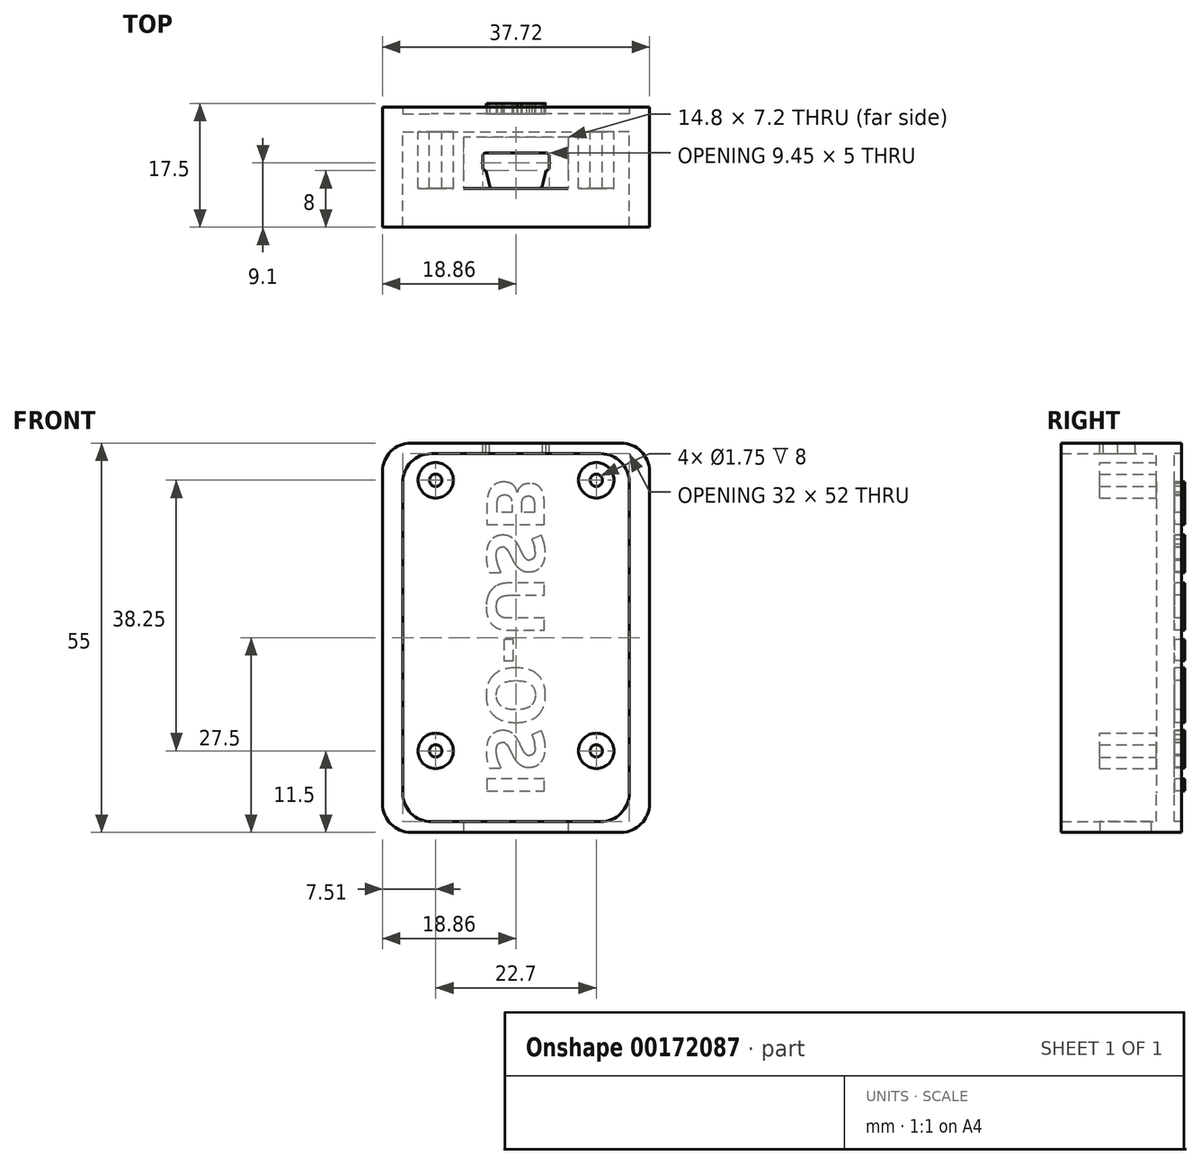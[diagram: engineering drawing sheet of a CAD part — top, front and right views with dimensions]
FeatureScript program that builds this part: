
annotation { "Feature Type Name" : "Feature", "Feature Type Description" : "" }
export const myFeature = defineFeature(function(context is Context, id is Id, definition is map)
    precondition{}
    {
        {
            var Q0;
            Q0=qCreatedBy(makeId("Front.planeOp"),FACE);
            var sketch = newSketch(context, id + "F0", { "sketchPlane" : qUnion([Q0])});
            skLineSegment(sketch, "E0.bottom", {"start": v(12, -26) * mm, "end": v(-12, -26) * mm});
            skLineSegment(sketch, "E0.top", {"start": v(12, 26) * mm, "end": v(-12, 26) * mm});
            skLineSegment(sketch, "E0.left", {"start": v(16, -22) * mm, "end": v(16, 22) * mm});
            skLineSegment(sketch, "E0.right", {"start": v(-16, -22) * mm, "end": v(-16, 22) * mm});
            skPoint(sketch, "E0.middle", {"position": v(0, 0) * mm});
            skPoint(sketch, "E1.visualSharp", {"position": v(-16, 26) * mm});
            skArc(sketch, "E1.filletArc", {"start": v(-12, 26) * mm, "mid": v(-14.83, 24.83) * mm, "end": v(-16, 22) * mm});
            skPoint(sketch, "E2.visualSharp", {"position": v(16, 26) * mm});
            skArc(sketch, "E2.filletArc", {"start": v(16, 22) * mm, "mid": v(14.83, 24.83) * mm, "end": v(12, 26) * mm});
            skPoint(sketch, "E3.visualSharp", {"position": v(16, -26) * mm});
            skArc(sketch, "E3.filletArc", {"start": v(12, -26) * mm, "mid": v(14.83, -24.83) * mm, "end": v(16, -22) * mm});
            skPoint(sketch, "E4.visualSharp", {"position": v(-16, -26) * mm});
            skArc(sketch, "E4.filletArc", {"start": v(-16, -22) * mm, "mid": v(-14.83, -24.83) * mm, "end": v(-12, -26) * mm});
            skLineSegment(sketch, "E5.bottom", {"start": v(14.86, -27.5) * mm, "end": v(-14.86, -27.5) * mm});
            skLineSegment(sketch, "E5.top", {"start": v(14.86, 27.5) * mm, "end": v(-14.86, 27.5) * mm});
            skLineSegment(sketch, "E5.left", {"start": v(18.86, -23.5) * mm, "end": v(18.86, 23.5) * mm});
            skLineSegment(sketch, "E5.right", {"start": v(-18.86, -23.5) * mm, "end": v(-18.86, 23.5) * mm});
            skPoint(sketch, "E6.visualSharp", {"position": v(-18.86, 27.5) * mm});
            skArc(sketch, "E6.filletArc", {"start": v(-14.86, 27.5) * mm, "mid": v(-17.69, 26.33) * mm, "end": v(-18.86, 23.5) * mm});
            skPoint(sketch, "E7.visualSharp", {"position": v(18.86, 27.5) * mm});
            skArc(sketch, "E7.filletArc", {"start": v(18.86, 23.5) * mm, "mid": v(17.69, 26.33) * mm, "end": v(14.86, 27.5) * mm});
            skPoint(sketch, "E8.visualSharp", {"position": v(18.86, -27.5) * mm});
            skArc(sketch, "E8.filletArc", {"start": v(14.86, -27.5) * mm, "mid": v(17.69, -26.33) * mm, "end": v(18.86, -23.5) * mm});
            skPoint(sketch, "E9.visualSharp", {"position": v(-18.86, -27.5) * mm});
            skArc(sketch, "E9.filletArc", {"start": v(-18.86, -23.5) * mm, "mid": v(-17.69, -26.33) * mm, "end": v(-14.86, -27.5) * mm});
            skCircle(sketch, "E10", {"center": v(-11.35, 22.25) * mm, "radius": 0.87 * mm});
            skLineSegment(sketch, "E11", {"start": v(0, 47.32) * mm, "end": v(0, -48.06) * mm});
            skCircle(sketch, "E12", {"center": v(11.35, 22.25) * mm, "radius": 0.88 * mm});
            skCircle(sketch, "E13", {"center": v(-11.35, -16) * mm, "radius": 0.88 * mm});
            skCircle(sketch, "E14", {"center": v(11.35, -16) * mm, "radius": 0.88 * mm});
            skCircle(sketch, "E15", {"center": v(11.35, 22.25) * mm, "radius": 2.5 * mm});
            skCircle(sketch, "E16", {"center": v(-11.35, 22.25) * mm, "radius": 2.5 * mm});
            skCircle(sketch, "E17", {"center": v(-11.35, -16) * mm, "radius": 2.5 * mm});
            skCircle(sketch, "E18", {"center": v(11.35, -16) * mm, "radius": 2.5 * mm});
            skSolve(sketch);
        }
        {
            var Q0;
            Q0=makeQuery(id+"F0.imprint","IMPRINT",FACE,{"disambiguationData":[TD([[makeQuery(id+"F0.imprint","IMPRINT",EDGE,{"derivedFrom":sQuery(id+"F0.wireOp",EDGE,"E0.right")}),1.0]])]});
            var Q1;
            Q1=makeQuery(id+"F0.imprint","IMPRINT",FACE,{"disambiguationData":[TD([[makeQuery(id+"F0.imprint","IMPRINT",EDGE,{"derivedFrom":sQuery(id+"F0.wireOp",EDGE,"E0.right")}),-1.0]])]});
            var Q2;
            Q2=makeQuery(id+"F0.imprint","IMPRINT",FACE,{"disambiguationData":[TD([[makeQuery(id+"F0.imprint","IMPRINT",EDGE,{"derivedFrom":sQuery(id+"F0.wireOp",EDGE,"E0.left")}),1.0]])]});
            var Q3;
            Q3=makeQuery(id+"F0.imprint","IMPRINT",FACE,{"disambiguationData":[TD([[makeQuery(id+"F0.imprint","IMPRINT",EDGE,{"derivedFrom":sQuery(id+"F0.wireOp",EDGE,"E0.left")}),-1.0]])]});
            var Q4;
            Q4=makeQuery(id+"F0.imprint","IMPRINT",FACE,{"disambiguationData":[TD([[makeQuery(id+"F0.imprint","IMPRINT",EDGE,{"derivedFrom":sQuery(id+"F0.wireOp",EDGE,"E12")}),-1.0]])]});
            var Q5;
            Q5=makeQuery(id+"F0.imprint","IMPRINT",FACE,{"disambiguationData":[TD([[makeQuery(id+"F0.imprint","IMPRINT",EDGE,{"derivedFrom":sQuery(id+"F0.wireOp",EDGE,"E10")}),-1.0]])]});
            var Q6;
            Q6=makeQuery(id+"F0.imprint","IMPRINT",FACE,{"disambiguationData":[TD([[makeQuery(id+"F0.imprint","IMPRINT",EDGE,{"derivedFrom":sQuery(id+"F0.wireOp",EDGE,"E10")}),1.0]])]});
            var Q7;
            Q7=makeQuery(id+"F0.imprint","IMPRINT",FACE,{"disambiguationData":[TD([[makeQuery(id+"F0.imprint","IMPRINT",EDGE,{"derivedFrom":sQuery(id+"F0.wireOp",EDGE,"E12")}),1.0]])]});
            var Q8;
            Q8=makeQuery(id+"F0.imprint","IMPRINT",FACE,{"disambiguationData":[TD([[makeQuery(id+"F0.imprint","IMPRINT",EDGE,{"derivedFrom":sQuery(id+"F0.wireOp",EDGE,"E13")}),-1.0]])]});
            var Q9;
            Q9=makeQuery(id+"F0.imprint","IMPRINT",FACE,{"disambiguationData":[TD([[makeQuery(id+"F0.imprint","IMPRINT",EDGE,{"derivedFrom":sQuery(id+"F0.wireOp",EDGE,"E13")}),1.0]])]});
            var Q10;
            Q10=makeQuery(id+"F0.imprint","IMPRINT",FACE,{"disambiguationData":[TD([[makeQuery(id+"F0.imprint","IMPRINT",EDGE,{"derivedFrom":sQuery(id+"F0.wireOp",EDGE,"E14")}),1.0]])]});
            var Q11;
            Q11=makeQuery(id+"F0.imprint","IMPRINT",FACE,{"disambiguationData":[TD([[makeQuery(id+"F0.imprint","IMPRINT",EDGE,{"derivedFrom":sQuery(id+"F0.wireOp",EDGE,"E14")}),-1.0]])]});
            extrude(context, id + "F1", {"entities" : qUnion([Q0, Q1, Q2, Q3, Q4, Q5, Q6, Q7, Q8, Q9, Q10, Q11]), "depth" : 2.5 * mm});
        }
        {
            var Q0;
            Q0=makeQuery(id+"F0.imprint","IMPRINT",FACE,{"disambiguationData":[TD([[makeQuery(id+"F0.imprint","IMPRINT",EDGE,{"derivedFrom":sQuery(id+"F0.wireOp",EDGE,"E0.right")}),1.0]])]});
            var Q1;
            Q1=makeQuery(id+"F0.imprint","IMPRINT",FACE,{"disambiguationData":[TD([[makeQuery(id+"F0.imprint","IMPRINT",EDGE,{"derivedFrom":sQuery(id+"F0.wireOp",EDGE,"E0.left")}),-1.0]])]});
            extrude(context, id + "F2", {"entities" : qUnion([Q0, Q1]), "operationType" : NewBodyOperationType.ADD, "depth" : 16 * mm});
        }
        {
            var Q0;
            Q0=makeQuery(id+"F0.imprint","IMPRINT",FACE,{"disambiguationData":[TD([[makeQuery(id+"F0.imprint","IMPRINT",EDGE,{"derivedFrom":sQuery(id+"F0.wireOp",EDGE,"E12")}),-1.0]])]});
            var Q1;
            Q1=makeQuery(id+"F0.imprint","IMPRINT",FACE,{"disambiguationData":[TD([[makeQuery(id+"F0.imprint","IMPRINT",EDGE,{"derivedFrom":sQuery(id+"F0.wireOp",EDGE,"E10")}),-1.0]])]});
            var Q2;
            Q2=makeQuery(id+"F0.imprint","IMPRINT",FACE,{"disambiguationData":[TD([[makeQuery(id+"F0.imprint","IMPRINT",EDGE,{"derivedFrom":sQuery(id+"F0.wireOp",EDGE,"E13")}),-1.0]])]});
            var Q3;
            Q3=makeQuery(id+"F0.imprint","IMPRINT",FACE,{"disambiguationData":[TD([[makeQuery(id+"F0.imprint","IMPRINT",EDGE,{"derivedFrom":sQuery(id+"F0.wireOp",EDGE,"E14")}),-1.0]])]});
            extrude(context, id + "F3", {"entities" : qUnion([Q0, Q1, Q2, Q3]), "operationType" : NewBodyOperationType.ADD, "depth" : 10.5 * mm});
        }
        {
            var Q0;
            Q0=makeQuery(id+"F0.imprint","IMPRINT",FACE,{"disambiguationData":[TD([[makeQuery(id+"F0.imprint","IMPRINT",EDGE,{"derivedFrom":sQuery(id+"F0.wireOp",EDGE,"E0.right")}),1.0]])]});
            var Q1;
            Q1=makeQuery(id+"F0.imprint","IMPRINT",FACE,{"disambiguationData":[TD([[makeQuery(id+"F0.imprint","IMPRINT",EDGE,{"derivedFrom":sQuery(id+"F0.wireOp",EDGE,"E0.left")}),-1.0]])]});
            extrude(context, id + "F4", {"entities" : qUnion([Q0, Q1]), "operationType" : NewBodyOperationType.ADD, "oppositeDirection" : true, "depth" : 1 * mm});
        }
        {
            var Q0;
            {var subQ0=sQuery(id+"F0.wireOp",EDGE,"E5.top");Q0=makeQuery(id+"F4.boolean.opBoolean","MERGE",FACE,{"derivedFrom":[makeQuery(id+"F2.boolean.opBoolean","MERGE",FACE,{"derivedFrom":[makeQuery(id+"F1.opExtrude","SWEPT_FACE",FACE,{"disambiguationData":[OSD([subQ0])]}),makeQuery(id+"F2.opExtrude","SWEPT_FACE",FACE,{"disambiguationData":[OSD([subQ0])]})]}),makeQuery(id+"F4.opExtrude","SWEPT_FACE",FACE,{"disambiguationData":[OSD([subQ0])]})]});}
            var sketch = newSketch(context, id + "F5", { "sketchPlane" : qUnion([Q0])});
            skLineSegment(sketch, "E19.bottom", {"start": v(3.25, -10.5) * mm, "end": v(-3.25, -10.5) * mm});
            skLineSegment(sketch, "E20.bottom", {"start": v(4.23, -5.5) * mm, "end": v(-4.23, -5.5) * mm});
            skLineSegment(sketch, "E20.left", {"start": v(4.73, -6) * mm, "end": v(4.73, -7.5) * mm});
            skLineSegment(sketch, "E20.right", {"start": v(-4.73, -6) * mm, "end": v(-4.73, -7.5) * mm});
            skPoint(sketch, "E21.visualSharp", {"position": v(-4.73, -5.5) * mm});
            skArc(sketch, "E21.filletArc", {"start": v(-4.23, -5.5) * mm, "mid": v(-4.58, -5.65) * mm, "end": v(-4.73, -6) * mm});
            skPoint(sketch, "E22.visualSharp", {"position": v(4.73, -5.5) * mm});
            skArc(sketch, "E22.filletArc", {"start": v(4.73, -6) * mm, "mid": v(4.58, -5.65) * mm, "end": v(4.23, -5.5) * mm});
            skPoint(sketch, "E23.visualSharp", {"position": v(3.75, -10.5) * mm});
            skArc(sketch, "E23.filletArc", {"start": v(3.25, -10.5) * mm, "mid": v(3.6, -10.35) * mm, "end": v(3.75, -10) * mm});
            skPoint(sketch, "E24.visualSharp", {"position": v(-3.75, -10.5) * mm});
            skArc(sketch, "E24.filletArc", {"start": v(-3.75, -10) * mm, "mid": v(-3.6, -10.35) * mm, "end": v(-3.25, -10.5) * mm});
            skPoint(sketch, "E25.visualSharp", {"position": v(-4.73, -8) * mm});
            skArc(sketch, "E25.filletArc", {"start": v(-4.73, -7.5) * mm, "mid": v(-4.58, -7.85) * mm, "end": v(-4.23, -8) * mm});
            skPoint(sketch, "E26.visualSharp", {"position": v(4.73, -8) * mm});
            skArc(sketch, "E26.filletArc", {"start": v(4.23, -8) * mm, "mid": v(4.58, -7.85) * mm, "end": v(4.73, -7.5) * mm});
            skLineSegment(sketch, "E27", {"start": v(-4.23, -8) * mm, "end": v(-3.75, -10) * mm});
            skLineSegment(sketch, "E28", {"start": v(4.23, -8) * mm, "end": v(3.75, -10) * mm});
            skPoint(sketch, "E19.top.end.orphan", {"position": v(-3.75, -8) * mm});
            skPoint(sketch, "E19.top.start.orphan", {"position": v(3.75, -9.5) * mm});
            skSolve(sketch);
        }
        {
            var Q0;
            Q0=makeQuery(id+"F5.imprint","IMPRINT",FACE,{"disambiguationData":[TD([[makeQuery(id+"F5.imprint","IMPRINT",EDGE,{"derivedFrom":sQuery(id+"F5.wireOp",EDGE,"E19.bottom")}),-1.0]])]});
            extrude(context, id + "F6", {"entities" : qUnion([Q0]), "operationType" : NewBodyOperationType.REMOVE, "oppositeDirection" : true, "depth" : 25 * mm});
        }
        {
            var Q0;
            {var subQ0=sQuery(id+"F0.wireOp",EDGE,"E5.bottom");Q0=makeQuery(id+"F4.boolean.opBoolean","MERGE",FACE,{"derivedFrom":[makeQuery(id+"F2.boolean.opBoolean","MERGE",FACE,{"derivedFrom":[makeQuery(id+"F1.opExtrude","SWEPT_FACE",FACE,{"disambiguationData":[OSD([subQ0])]}),makeQuery(id+"F2.opExtrude","SWEPT_FACE",FACE,{"disambiguationData":[OSD([subQ0])]})]}),makeQuery(id+"F4.opExtrude","SWEPT_FACE",FACE,{"disambiguationData":[OSD([subQ0])]})]});}
            var sketch = newSketch(context, id + "F7", { "sketchPlane" : qUnion([Q0])});
            skLineSegment(sketch, "E29.bottom", {"start": v(7.4, 3.3) * mm, "end": v(-7.4, 3.3) * mm});
            skLineSegment(sketch, "E29.top", {"start": v(7.4, 10.5) * mm, "end": v(-7.4, 10.5) * mm});
            skLineSegment(sketch, "E29.left", {"start": v(7.4, 3.3) * mm, "end": v(7.4, 10.5) * mm});
            skLineSegment(sketch, "E29.right", {"start": v(-7.4, 3.3) * mm, "end": v(-7.4, 10.5) * mm});
            skPoint(sketch, "E29.middle", {"position": v(0, 6.9) * mm});
            skSolve(sketch);
        }
        {
            var Q0;
            Q0=makeQuery(id+"F7.imprint","IMPRINT",FACE,{"disambiguationData":[TD([[makeQuery(id+"F7.imprint","IMPRINT",EDGE,{"derivedFrom":sQuery(id+"F7.wireOp",EDGE,"E29.bottom")}),-1.0]])]});
            extrude(context, id + "F8", {"entities" : qUnion([Q0]), "operationType" : NewBodyOperationType.REMOVE, "oppositeDirection" : true, "depth" : 25 * mm});
        }
        {
            var Q0;
            {var subQ0=sQuery(id+"F0.wireOp",EDGE,"E8.filletArc");var subQ1=sQuery(id+"F0.wireOp",EDGE,"E5.left");Q0=makeQuery(id+"F4.boolean.opBoolean","MERGE",EDGE,{"derivedFrom":[makeQuery(id+"F2.boolean.opBoolean","MERGE",EDGE,{"derivedFrom":[makeQuery(id+"F1.opExtrude","SWEPT_EDGE",EDGE,{"disambiguationData":[OSD([subQ1,subQ0])]}),makeQuery(id+"F2.opExtrude","SWEPT_EDGE",EDGE,{"disambiguationData":[OSD([subQ1,subQ0])]})]}),makeQuery(id+"F4.opExtrude","SWEPT_EDGE",EDGE,{"disambiguationData":[OSD([subQ1,subQ0])]})]});}
            cPlane(context, id + "F9", {"entities" : qUnion([Q0]), "cplaneType" : CPlaneType.MID_PLANE, "offset" : 25 * mm, "flipAlignment" : true, "width" : 150 * mm, "height" : 150 * mm});
        }
        {
            var Q0;
            Q0=qCreatedBy(id+"F9.planeOp",FACE);
            var sketch = newSketch(context, id + "F10", { "sketchPlane" : qUnion([Q0])});
            skText(sketch, "E30", { "text": "ISO-USB\n", "fontName": "OpenSans-Bold.ttf"});
            const initialGuessF10  = {"E30": [0.0041, -0.0227, 0, 1, 0.0082]};
            skSetInitialGuess(sketch, initialGuessF10);
            skSolve(sketch);
        }
        {
            var Q0;
            Q0 = qSketchRegion(id + "F10", true);
            extrude(context, id + "F11", {"entities" : qUnion([Q0]), "operationType" : NewBodyOperationType.ADD, "depth" : 9 * mm, "hasSecondDirection" : true, "secondDirectionOppositeDirection" : false, "secondDirectionDepth" : 5 * mm});
        }
    });
